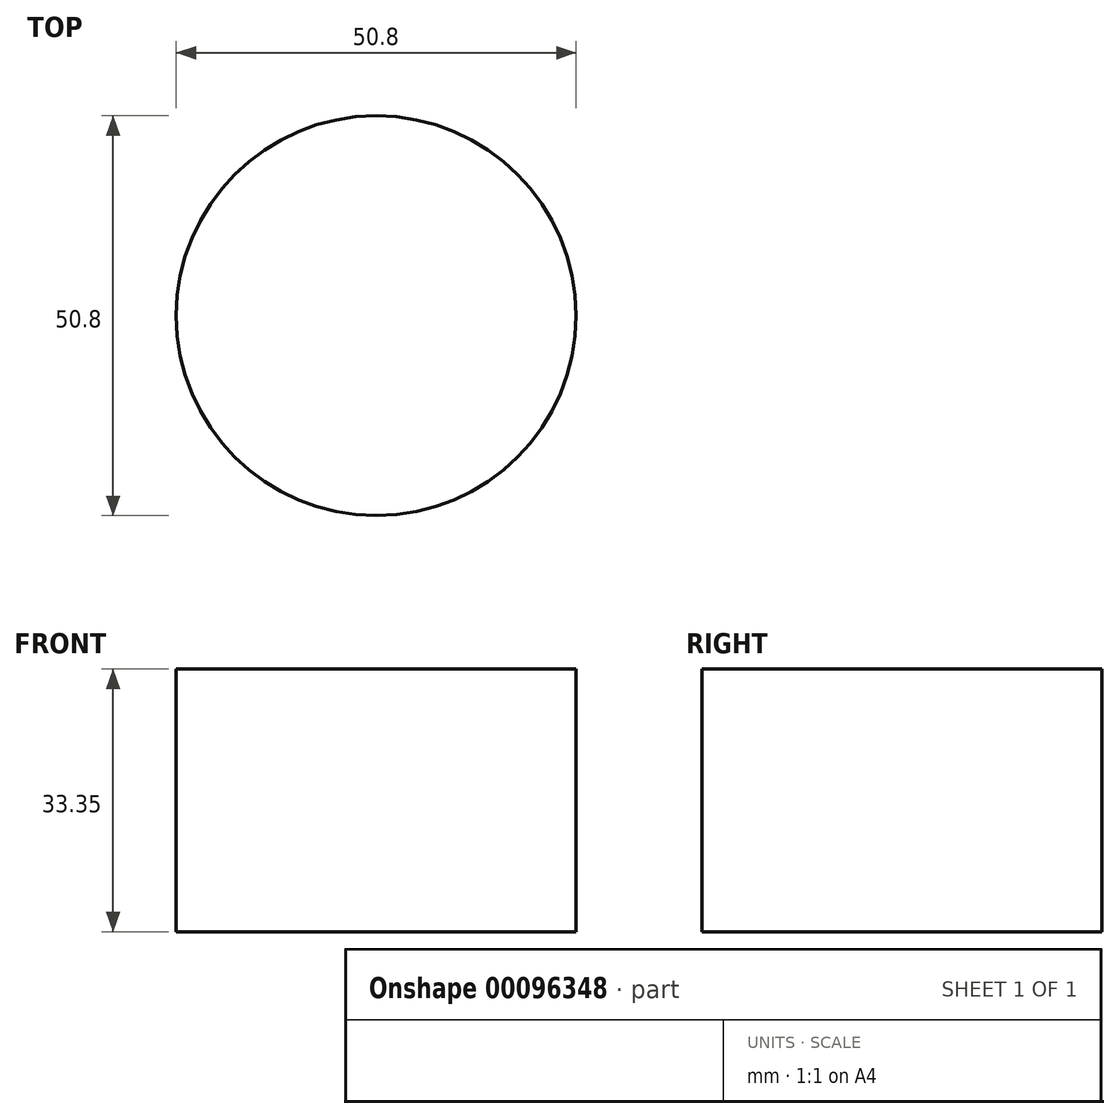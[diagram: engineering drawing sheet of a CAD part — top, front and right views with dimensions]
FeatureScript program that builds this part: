
annotation { "Feature Type Name" : "Feature", "Feature Type Description" : "" }
export const myFeature = defineFeature(function(context is Context, id is Id, definition is map)
    precondition{}
    {
        {
            var Q0;
            Q0=qCreatedBy(makeId("Top.planeOp"),FACE);
            var sketch = newSketch(context, id + "F0", { "sketchPlane" : qUnion([Q0])});
            skCircle(sketch, "E0", {"center": v(0, 0) * mm, "radius": 25.4 * mm});
            skSolve(sketch);
        }
        {
            var Q0;
            Q0 = qSketchRegion(id + "F0", true);
            extrude(context, id + "F1", {"entities" : qUnion([Q0]), "depth" : 33.35 * mm});
        }
    });
